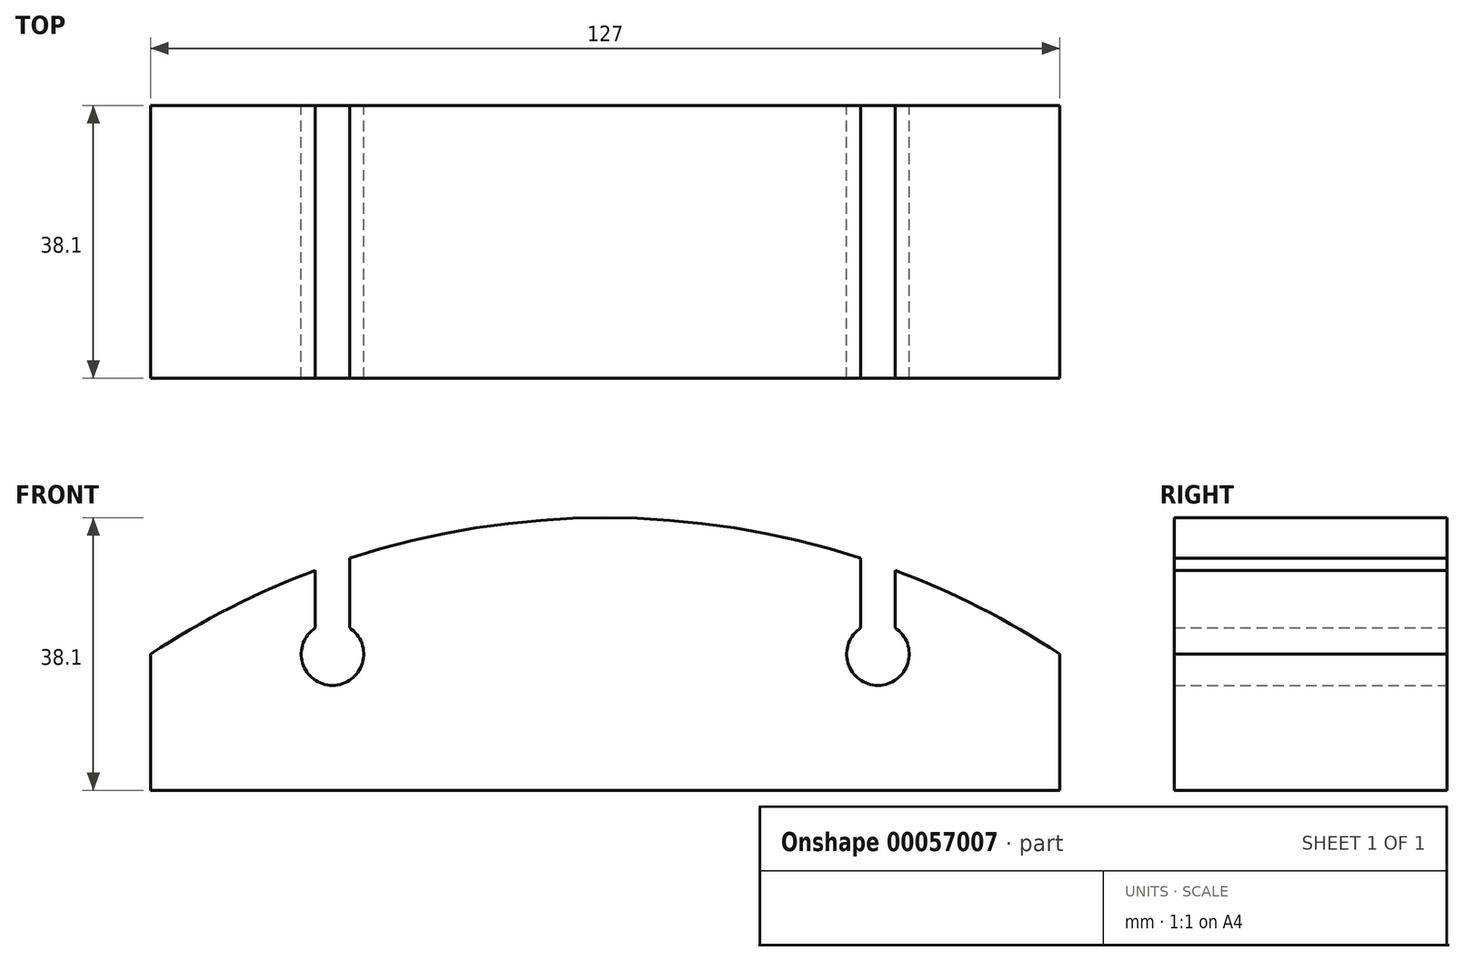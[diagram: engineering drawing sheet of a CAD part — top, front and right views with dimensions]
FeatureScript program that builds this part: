
annotation { "Feature Type Name" : "Feature", "Feature Type Description" : "" }
export const myFeature = defineFeature(function(context is Context, id is Id, definition is map)
    precondition{}
    {
        {
            var Q0;
            Q0=qCreatedBy(makeId("Front.planeOp"),FACE);
            var sketch = newSketch(context, id + "F0", { "sketchPlane" : qUnion([Q0])});
            skLineSegment(sketch, "E0.top", {"start": v(-65.22, -12.03) * mm, "end": v(61.78, -12.03) * mm});
            skLineSegment(sketch, "E0.left", {"start": v(-65.22, 7.02) * mm, "end": v(-65.22, -12.03) * mm});
            skLineSegment(sketch, "E0.right", {"start": v(61.78, 7.02) * mm, "end": v(61.78, -12.03) * mm});
            skArc(sketch, "E1", {"start": v(61.78, 7.02) * mm, "mid": v(50.6, 13.52) * mm, "end": v(38.77, 18.73) * mm});
            skArc(sketch, "E2", {"start": v(34, 10.68) * mm, "mid": v(36.38, 2.65) * mm, "end": v(38.77, 10.68) * mm});
            skLineSegment(sketch, "E3.rect.left", {"start": v(34, 20.4) * mm, "end": v(34, 10.68) * mm});
            skLineSegment(sketch, "E3.rect.right", {"start": v(38.77, 18.73) * mm, "end": v(38.77, 10.68) * mm});
            skArc(sketch, "E4", {"start": v(-42.2, 10.68) * mm, "mid": v(-39.82, 2.65) * mm, "end": v(-37.43, 10.68) * mm});
            skLineSegment(sketch, "E5.rect.left", {"start": v(-37.43, 20.4) * mm, "end": v(-37.43, 10.68) * mm});
            skLineSegment(sketch, "E5.rect.right", {"start": v(-42.2, 18.73) * mm, "end": v(-42.2, 10.68) * mm});
            skPoint(sketch, "E6.orphan", {"position": v(-42.2, 24.04) * mm});
            skPoint(sketch, "E7.orphan", {"position": v(-37.43, 24.04) * mm});
            skPoint(sketch, "E8.orphan", {"position": v(-42.2, -10) * mm});
            skPoint(sketch, "E9.orphan", {"position": v(-37.43, -10) * mm});
            skPoint(sketch, "E3.rect.top.start.orphan", {"position": v(34, -8.35) * mm});
            skPoint(sketch, "E10.orphan", {"position": v(38.77, -8.35) * mm});
            skPoint(sketch, "E11.orphan", {"position": v(38.77, 22.39) * mm});
            skPoint(sketch, "E12.orphan", {"position": v(34, 22.39) * mm});
            skArc(sketch, "E13.trimOffspring", {"start": v(34, 20.4) * mm, "mid": v(-1.72, 26.07) * mm, "end": v(-37.43, 20.4) * mm});
            skArc(sketch, "E14.trimOffspring", {"start": v(-42.2, 18.73) * mm, "mid": v(-54.04, 13.52) * mm, "end": v(-65.22, 7.02) * mm});
            skSolve(sketch);
        }
        {
            var Q0;
            Q0=makeQuery(id+"F0.imprint","IMPRINT",FACE,{"disambiguationData":[TD([[makeQuery(id+"F0.imprint","IMPRINT",EDGE,{"derivedFrom":sQuery(id+"F0.wireOp",EDGE,"E0.top")}),1.0]])]});
            extrude(context, id + "F1", {"entities" : qUnion([Q0]), "endBound" : BoundingType.SYMMETRIC, "depth" : 38.1 * mm});
        }
    });
